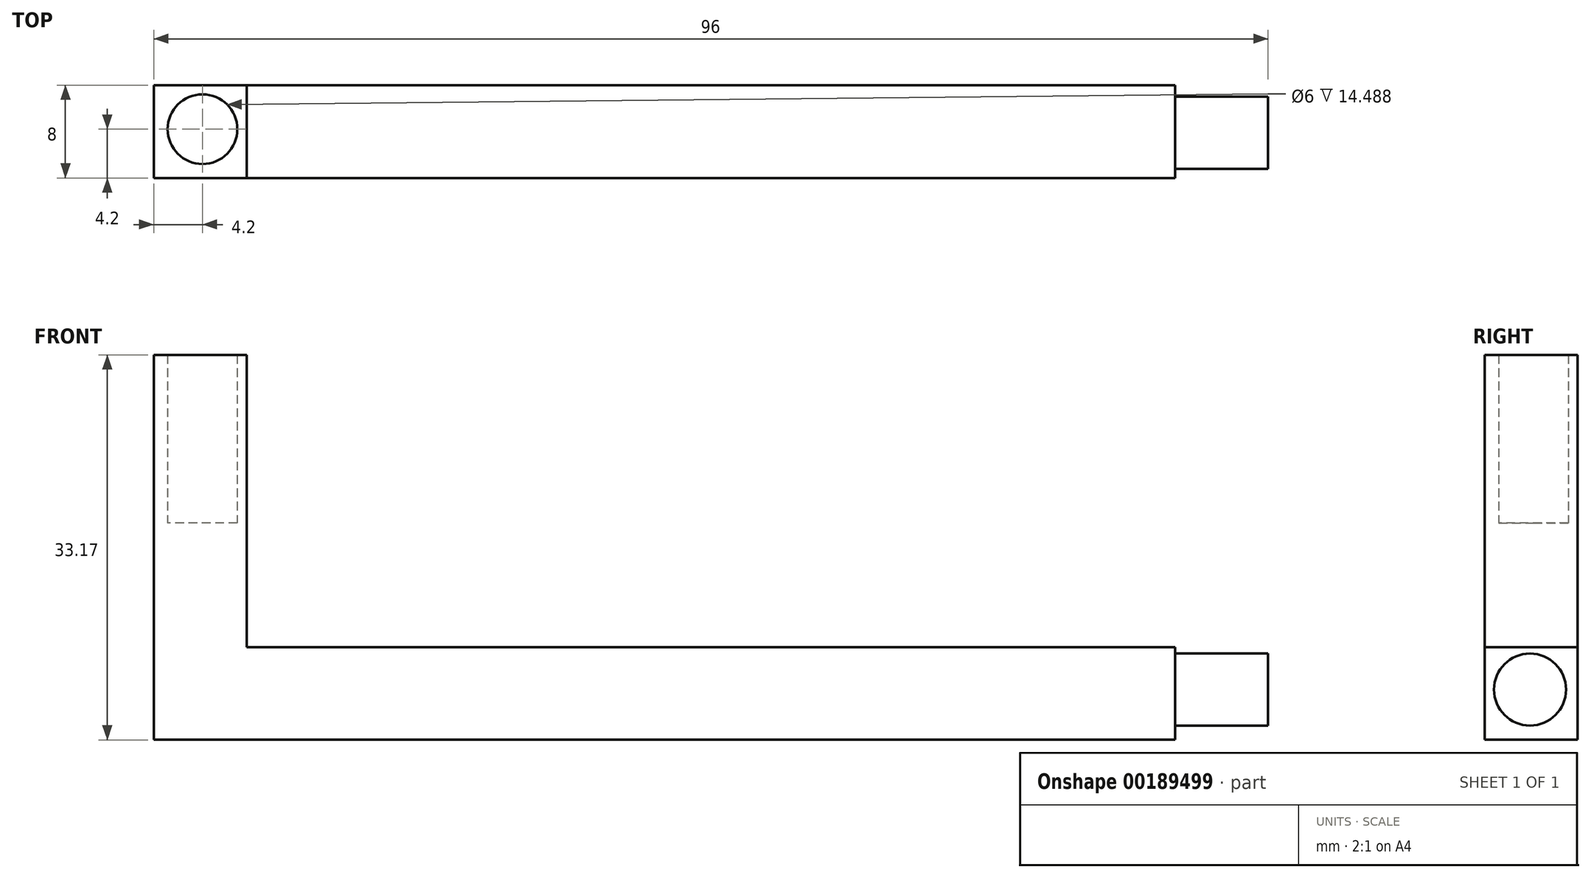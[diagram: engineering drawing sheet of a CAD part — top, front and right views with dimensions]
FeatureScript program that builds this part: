
annotation { "Feature Type Name" : "Feature", "Feature Type Description" : "" }
export const myFeature = defineFeature(function(context is Context, id is Id, definition is map)
    precondition{}
    {
        {
            var Q0;
            Q0=qCreatedBy(makeId("Front.planeOp"),FACE);
            var sketch = newSketch(context, id + "F0", { "sketchPlane" : qUnion([Q0])});
            skLineSegment(sketch, "E0", {"start": v(-80, 14.49) * mm, "end": v(-80, -10.68) * mm});
            skLineSegment(sketch, "E1", {"start": v(-80, -10.68) * mm, "end": v(0, -10.68) * mm});
            skLineSegment(sketch, "E2.0", {"start": v(-88, -18.68) * mm, "end": v(0, -18.68) * mm});
            skLineSegment(sketch, "E2.1", {"start": v(-88, 14.49) * mm, "end": v(-88, -18.68) * mm});
            skLineSegment(sketch, "E3", {"start": v(-88, 14.49) * mm, "end": v(-80, 14.49) * mm});
            skLineSegment(sketch, "E4", {"start": v(0, -10.68) * mm, "end": v(0, -18.68) * mm});
            skSolve(sketch);
        }
        {
            var Q0;
            Q0 = qSketchRegion(id + "F0", true);
            extrude(context, id + "F1", {"entities" : qUnion([Q0]), "depth" : 8 * mm});
        }
        {
            var Q0;
            Q0=qCreatedBy(makeId("Right.planeOp"),FACE);
            var sketch = newSketch(context, id + "F2", { "sketchPlane" : qUnion([Q0])});
            skCircle(sketch, "E5", {"center": v(-4.1, -14.34) * mm, "radius": 3.1 * mm});
            skSolve(sketch);
        }
        {
            var Q0;
            Q0=makeQuery(id+"F2.imprint","IMPRINT",FACE,{"disambiguationData":[TD([[makeQuery(id+"F2.imprint","IMPRINT",EDGE,{"derivedFrom":sQuery(id+"F2.wireOp",EDGE,"E5")}),1.0]])]});
            extrude(context, id + "F3", {"entities" : qUnion([Q0]), "operationType" : NewBodyOperationType.ADD, "depth" : 8 * mm});
        }
        {
            var Q0;
            Q0=qCreatedBy(makeId("Top.planeOp"),FACE);
            var sketch = newSketch(context, id + "F4", { "sketchPlane" : qUnion([Q0])});
            skCircle(sketch, "E6", {"center": v(-83.8, -3.8) * mm, "radius": 3 * mm});
            skSolve(sketch);
        }
        {
            var Q0;
            Q0 = qSketchRegion(id + "F4", true);
            extrude(context, id + "F5", {"entities" : qUnion([Q0]), "operationType" : NewBodyOperationType.REMOVE, "depth" : 16 * mm});
        }
    });
